# Revit family: Divider_Curtain-PSS-4050-Center_Drive
name_source: partatom
category: Specialty Equipment
revit_build: Autodesk Revit 2017 (Build: 20170816_0615(x64)
units: mm (PartAtom-declared; Revit-internal decimal feet)

## family parameters
Always vertical = Yes
Cut with Voids When Loaded = No
OmniClass Number = 23.40.50.34.17
OmniClass Title = Gymnasium Dividers
Part Type = Normal
Room Calculation Point = No
Round Connector Dimension = Use Diameter
Shared = No
Work Plane-Based = No

## types (1)
- 72'-0" x 24'-0"
    Assembly Code = E1020900
    Attachment Height = 24' - 6"
    BIM Version = v3.1
    Bridge Pipe Requirement = Bridge Pipe required when structure exceeds 14' span
    CSI MasterFormat = 11 66 53
    Carrier Center Spacing = 9' - 0"
    Curtain Lower Material = Vinyl Coated Fabric - Performance Sports Systems - C04 Royal Blue
    Curtain Lower Material Height = 11' - 11"
    Curtain Upper Material = Vinyl Mesh - Performance Sports Systems - M01 White
    Description = Center-Drive Divider Curtain
    Dim End to First Carriers = 6"
    Dual Motor Note = Dual Motors required on Curtains over 40' Long
    Height = 24' - 0"
    Length = 72' - 0"
    Manufacturer = Performance Sports Systems
    Maximum Size Limitations = 40' Max. Height; 120' Max. Length
    Model = 4050
    Motor Left End = Yes
    Motor Right End = Yes
    Product Page URL = http://www.perfsports.com
    Single Motor Note = Motor can be mounted at either end of Curtain
    Superstructure Finish = Powder Coat - Performance Sports Systems - Black
    URL = http://www.perfsports.com

## geometry (parser evidence)
native form markers: Blend x100, Sweep x15
no freeform markers — native parametric forms only
